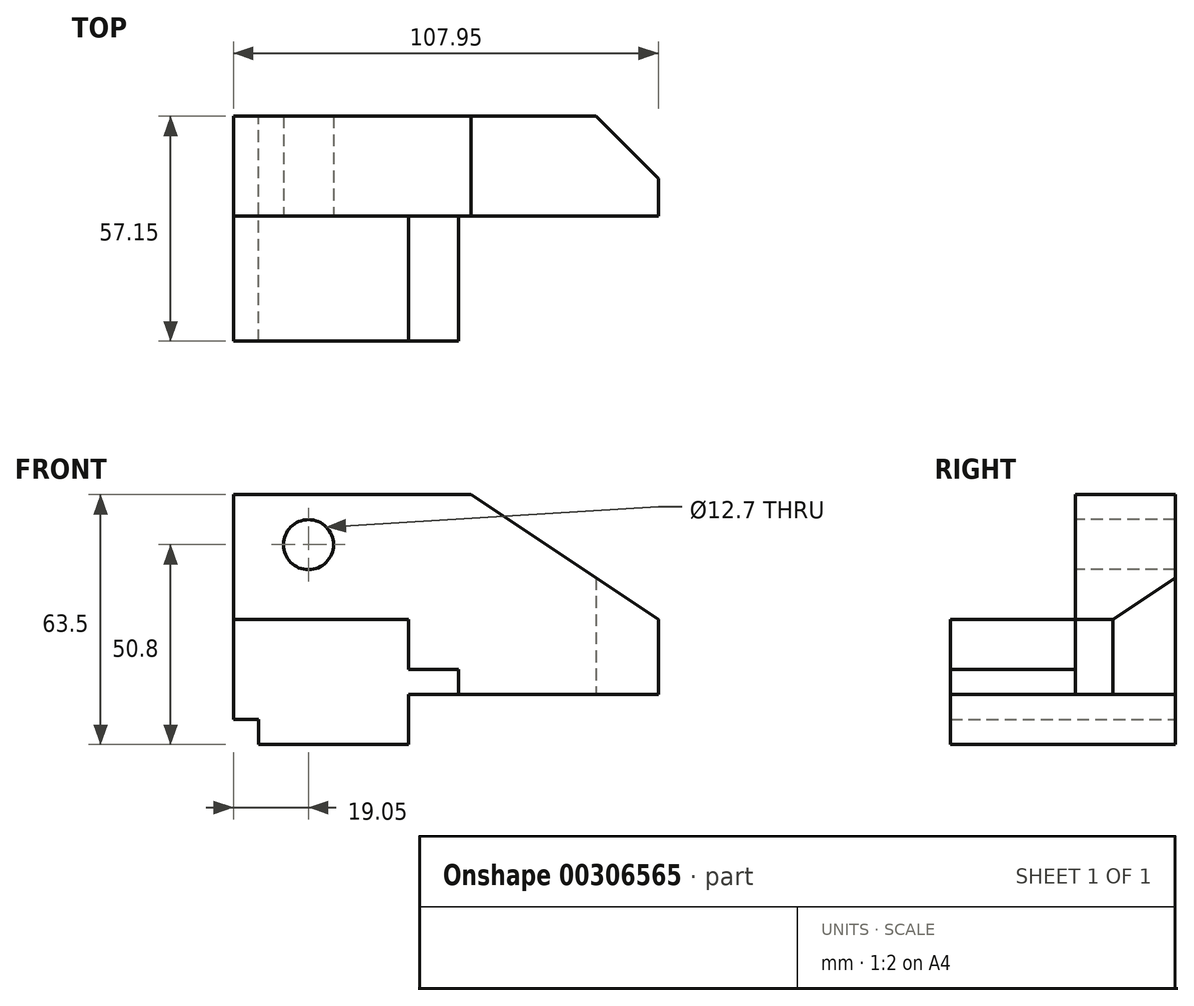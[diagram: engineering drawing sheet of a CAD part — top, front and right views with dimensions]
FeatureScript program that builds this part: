
annotation { "Feature Type Name" : "Feature", "Feature Type Description" : "" }
export const myFeature = defineFeature(function(context is Context, id is Id, definition is map)
    precondition{}
    {
        {
            var Q0;
            Q0=qCreatedBy(makeId("Front.planeOp"),FACE);
            var sketch = newSketch(context, id + "F0", { "sketchPlane" : qUnion([Q0])});
            skLineSegment(sketch, "E0", {"start": v(0, 0) * mm, "end": v(0, 6.35) * mm});
            skLineSegment(sketch, "E1", {"start": v(0, 6.35) * mm, "end": v(-6.35, 6.35) * mm});
            skLineSegment(sketch, "E2", {"start": v(-6.35, 6.35) * mm, "end": v(-6.35, 69.85) * mm});
            skLineSegment(sketch, "E3", {"start": v(0, 0) * mm, "end": v(101.6, 0) * mm});
            skLineSegment(sketch, "E4", {"start": v(101.6, 0) * mm, "end": v(101.6, 31.75) * mm});
            skLineSegment(sketch, "E5", {"start": v(-6.35, 69.85) * mm, "end": v(44.45, 69.85) * mm});
            skLineSegment(sketch, "E6", {"start": v(44.45, 69.85) * mm, "end": v(101.6, 31.75) * mm});
            skSolve(sketch);
        }
        {
            var Q0;
            Q0 = qSketchRegion(id + "F0", true);
            extrude(context, id + "F1", {"entities" : qUnion([Q0]), "endBound" : BoundingType.SYMMETRIC, "depth" : 57.15 * mm});
        }
        {
            var Q0;
            Q0=makeQuery(id+"F1.opExtrude","CAP_FACE",FACE,{"disambiguationData":[OSD([sQuery(id+"F0.wireOp",EDGE,"E0"),sQuery(id+"F0.wireOp",EDGE,"E1"),sQuery(id+"F0.wireOp",EDGE,"E2"),sQuery(id+"F0.wireOp",EDGE,"E3"),sQuery(id+"F0.wireOp",EDGE,"E4"),sQuery(id+"F0.wireOp",EDGE,"E5"),sQuery(id+"F0.wireOp",EDGE,"E6")])],"isStart":false});
            var sketch = newSketch(context, id + "F2", { "sketchPlane" : qUnion([Q0])});
            skLineSegment(sketch, "E7", {"start": v(101.6, 0) * mm, "end": v(38.1, 0) * mm});
            skLineSegment(sketch, "E8", {"start": v(38.1, 0) * mm, "end": v(38.1, 12.7) * mm});
            skLineSegment(sketch, "E9", {"start": v(38.1, 12.7) * mm, "end": v(50.8, 12.7) * mm});
            skLineSegment(sketch, "E10", {"start": v(50.8, 12.7) * mm, "end": v(50.8, 19.05) * mm});
            skLineSegment(sketch, "E11", {"start": v(50.8, 19.05) * mm, "end": v(38.1, 19.05) * mm});
            skLineSegment(sketch, "E12", {"start": v(38.1, 19.05) * mm, "end": v(38.1, 31.75) * mm});
            skLineSegment(sketch, "E13", {"start": v(38.1, 31.75) * mm, "end": v(-6.35, 31.75) * mm});
            skLineSegment(sketch, "E14", {"start": v(-6.35, 31.75) * mm, "end": v(-6.35, 69.85) * mm});
            skLineSegment(sketch, "E15", {"start": v(-6.35, 69.85) * mm, "end": v(44.45, 69.85) * mm});
            skLineSegment(sketch, "E16", {"start": v(44.45, 69.85) * mm, "end": v(101.6, 31.75) * mm});
            skLineSegment(sketch, "E17", {"start": v(101.6, 31.75) * mm, "end": v(101.6, 0) * mm});
            skSolve(sketch);
        }
        {
            var Q0;
            Q0=makeQuery(id+"F2.imprint","IMPRINT",FACE,{"disambiguationData":[TD([[makeQuery(id+"F2.imprint","IMPRINT",EDGE,{"derivedFrom":sQuery(id+"F2.wireOp",EDGE,"E7")}),1.0]])]});
            extrude(context, id + "F3", {"entities" : qUnion([Q0]), "operationType" : NewBodyOperationType.REMOVE, "oppositeDirection" : true, "depth" : 31.75 * mm});
        }
        {
            var Q0;
            Q0=makeQuery(id+"F1.opExtrude","SWEPT_FACE",FACE,{"disambiguationData":[OSD([sQuery(id+"F0.wireOp",EDGE,"E3")])]});
            var sketch = newSketch(context, id + "F4", { "sketchPlane" : qUnion([Q0])});
            skLineSegment(sketch, "E18", {"start": v(101.6, -28.58) * mm, "end": v(85.73, -28.58) * mm});
            skLineSegment(sketch, "E19", {"start": v(85.73, -28.58) * mm, "end": v(101.6, -12.7) * mm});
            skLineSegment(sketch, "E20", {"start": v(101.6, -12.7) * mm, "end": v(101.6, -28.58) * mm});
            skSolve(sketch);
        }
        {
            var Q0;
            Q0 = qSketchRegion(id + "F4", true);
            extrude(context, id + "F5", {"entities" : qUnion([Q0]), "operationType" : NewBodyOperationType.REMOVE, "endBound" : BoundingType.THROUGH_ALL, "oppositeDirection" : true, "depth" : 25.4 * mm});
        }
        {
            var Q0;
            Q0=makeQuery(id+"F3.boolean.opBoolean","COPY",FACE,{"derivedFrom":makeQuery(id+"F3.opExtrude","CAP_FACE",FACE,{"disambiguationData":[OSD([sQuery(id+"F2.wireOp",EDGE,"E7"),sQuery(id+"F2.wireOp",EDGE,"E8"),sQuery(id+"F2.wireOp",EDGE,"E9"),sQuery(id+"F2.wireOp",EDGE,"E10"),sQuery(id+"F2.wireOp",EDGE,"E11"),sQuery(id+"F2.wireOp",EDGE,"E12"),sQuery(id+"F2.wireOp",EDGE,"E13"),sQuery(id+"F2.wireOp",EDGE,"E14"),sQuery(id+"F2.wireOp",EDGE,"E15"),sQuery(id+"F2.wireOp",EDGE,"E16"),sQuery(id+"F2.wireOp",EDGE,"E17")])],"isStart":false})});
            var sketch = newSketch(context, id + "F6", { "sketchPlane" : qUnion([Q0])});
            skCircle(sketch, "E21", {"center": v(12.7, 50.8) * mm, "radius": 6.35 * mm});
            skSolve(sketch);
        }
        {
            var Q0;
            Q0 = qSketchRegion(id + "F6", true);
            extrude(context, id + "F7", {"entities" : qUnion([Q0]), "operationType" : NewBodyOperationType.REMOVE, "endBound" : BoundingType.THROUGH_ALL, "oppositeDirection" : true, "depth" : 25.4 * mm});
        }
        {
            var Q0;
            Q0=makeQuery(id+"F3.boolean.opBoolean","COPY",FACE,{"derivedFrom":makeQuery(id+"F3.opExtrude","CAP_FACE",FACE,{"disambiguationData":[OSD([sQuery(id+"F2.wireOp",EDGE,"E7"),sQuery(id+"F2.wireOp",EDGE,"E8"),sQuery(id+"F2.wireOp",EDGE,"E9"),sQuery(id+"F2.wireOp",EDGE,"E10"),sQuery(id+"F2.wireOp",EDGE,"E11"),sQuery(id+"F2.wireOp",EDGE,"E12"),sQuery(id+"F2.wireOp",EDGE,"E13"),sQuery(id+"F2.wireOp",EDGE,"E14"),sQuery(id+"F2.wireOp",EDGE,"E15"),sQuery(id+"F2.wireOp",EDGE,"E16"),sQuery(id+"F2.wireOp",EDGE,"E17")])],"isStart":false})});
            var sketch = newSketch(context, id + "F8", { "sketchPlane" : qUnion([Q0])});
            skLineSegment(sketch, "E22", {"start": v(38.1, 0) * mm, "end": v(101.6, 0) * mm});
            skLineSegment(sketch, "E23", {"start": v(101.6, 0) * mm, "end": v(101.6, 12.7) * mm});
            skPoint(sketch, "E23.endSnap0", {"position": v(101.6, 15.88) * mm});
            skLineSegment(sketch, "E24", {"start": v(101.6, 12.7) * mm, "end": v(50.8, 12.7) * mm});
            skLineSegment(sketch, "E25", {"start": v(50.8, 12.7) * mm, "end": v(38.1, 12.7) * mm});
            skLineSegment(sketch, "E26", {"start": v(38.1, 12.7) * mm, "end": v(38.1, 0) * mm});
            skSolve(sketch);
        }
        {
            var Q0;
            Q0 = qSketchRegion(id + "F8", true);
            extrude(context, id + "F9", {"entities" : qUnion([Q0]), "operationType" : NewBodyOperationType.REMOVE, "endBound" : BoundingType.THROUGH_ALL, "oppositeDirection" : true, "depth" : 25.4 * mm});
        }
        {
            var Q0;
            Q0=makeQuery(id+"F3.boolean.opBoolean","COPY",FACE,{"derivedFrom":makeQuery(id+"F3.opExtrude","CAP_FACE",FACE,{"disambiguationData":[OSD([sQuery(id+"F2.wireOp",EDGE,"E7"),sQuery(id+"F2.wireOp",EDGE,"E8"),sQuery(id+"F2.wireOp",EDGE,"E9"),sQuery(id+"F2.wireOp",EDGE,"E10"),sQuery(id+"F2.wireOp",EDGE,"E11"),sQuery(id+"F2.wireOp",EDGE,"E12"),sQuery(id+"F2.wireOp",EDGE,"E13"),sQuery(id+"F2.wireOp",EDGE,"E14"),sQuery(id+"F2.wireOp",EDGE,"E15"),sQuery(id+"F2.wireOp",EDGE,"E16"),sQuery(id+"F2.wireOp",EDGE,"E17")])],"isStart":false})});
            var sketch = newSketch(context, id + "F10", { "sketchPlane" : qUnion([Q0])});
            skLineSegment(sketch, "E27", {"start": v(-6.35, 69.85) * mm, "end": v(-6.35, 63.5) * mm});
            skLineSegment(sketch, "E28", {"start": v(-6.35, 63.5) * mm, "end": v(53.97, 63.5) * mm});
            skLineSegment(sketch, "E29", {"start": v(53.97, 63.5) * mm, "end": v(44.45, 69.85) * mm});
            skLineSegment(sketch, "E30", {"start": v(44.45, 69.85) * mm, "end": v(-6.35, 69.85) * mm});
            skSolve(sketch);
        }
        {
            var Q0;
            Q0 = qSketchRegion(id + "F10", true);
            extrude(context, id + "F11", {"entities" : qUnion([Q0]), "operationType" : NewBodyOperationType.REMOVE, "endBound" : BoundingType.THROUGH_ALL, "oppositeDirection" : true, "depth" : 25.4 * mm});
        }
    });
